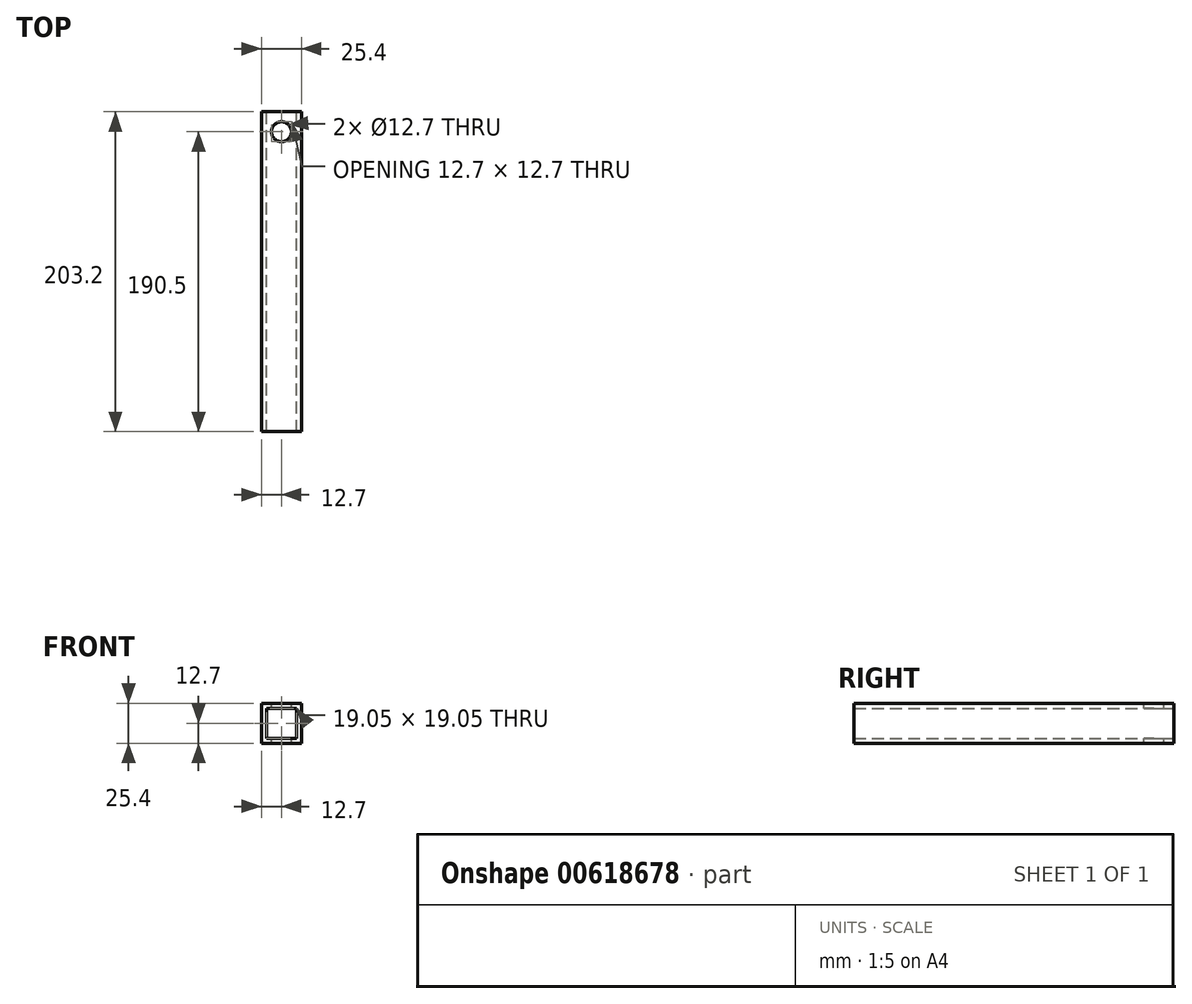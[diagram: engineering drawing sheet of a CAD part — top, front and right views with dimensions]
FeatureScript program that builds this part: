
annotation { "Feature Type Name" : "Feature", "Feature Type Description" : "" }
export const myFeature = defineFeature(function(context is Context, id is Id, definition is map)
    precondition{}
    {
        {
            var Q0;
            Q0=qCreatedBy(makeId("Front.planeOp"),FACE);
            var sketch = newSketch(context, id + "F0", { "sketchPlane" : qUnion([Q0])});
            skLineSegment(sketch, "E0.bottom", {"start": v(12.7, 12.7) * mm, "end": v(-12.7, 12.7) * mm});
            skLineSegment(sketch, "E0.top", {"start": v(12.7, -12.7) * mm, "end": v(-12.7, -12.7) * mm});
            skLineSegment(sketch, "E0.left", {"start": v(12.7, 12.7) * mm, "end": v(12.7, -12.7) * mm});
            skLineSegment(sketch, "E0.right", {"start": v(-12.7, 12.7) * mm, "end": v(-12.7, -12.7) * mm});
            skPoint(sketch, "E0.middle", {"position": v(0, 0) * mm});
            skLineSegment(sketch, "E1.bottom", {"start": v(9.53, 9.53) * mm, "end": v(-9.53, 9.53) * mm});
            skLineSegment(sketch, "E1.top", {"start": v(9.53, -9.53) * mm, "end": v(-9.53, -9.53) * mm});
            skLineSegment(sketch, "E1.left", {"start": v(9.53, 9.53) * mm, "end": v(9.53, -9.53) * mm});
            skLineSegment(sketch, "E1.right", {"start": v(-9.53, 9.53) * mm, "end": v(-9.53, -9.53) * mm});
            skSolve(sketch);
        }
        {
            var Q0;
            Q0=makeQuery(id+"F0.imprint","IMPRINT",FACE,{"disambiguationData":[TD([[makeQuery(id+"F0.imprint","IMPRINT",EDGE,{"derivedFrom":sQuery(id+"F0.wireOp",EDGE,"E0.bottom")}),1.0]])]});
            extrude(context, id + "F1", {"entities" : qUnion([Q0]), "depth" : 203.2 * mm, "offsetDistance" : 25.4 * mm});
        }
        {
            var Q0;
            Q0=makeQuery(id+"F1.opExtrude","SWEPT_FACE",FACE,{"disambiguationData":[OSD([sQuery(id+"F0.wireOp",EDGE,"E0.bottom")])]});
            var sketch = newSketch(context, id + "F2", { "sketchPlane" : qUnion([Q0])});
            skCircle(sketch, "E2", {"center": v(0, -12.7) * mm, "radius": 6.35 * mm});
            skSolve(sketch);
        }
        {
            var Q0;
            Q0=makeQuery(id+"F2.imprint","IMPRINT",FACE,{"disambiguationData":[TD([[makeQuery(id+"F2.imprint","IMPRINT",EDGE,{"derivedFrom":sQuery(id+"F2.wireOp",EDGE,"E2")}),1.0]])]});
            extrude(context, id + "F3", {"entities" : qUnion([Q0]), "operationType" : NewBodyOperationType.REMOVE, "oppositeDirection" : true, "depth" : 25.4 * mm, "offsetDistance" : 25.4 * mm});
        }
    });
